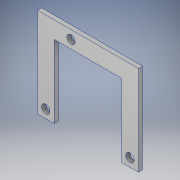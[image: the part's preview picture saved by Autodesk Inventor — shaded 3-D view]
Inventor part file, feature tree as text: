
AUTODESK INVENTOR PART (.ipt)
format: ipt  version: 2018.1 (Build 221171000, 171)  size: 120,832 bytes
history: native  units: mm
features: extrude x2, sketch x2, other x1
ambient origin geometry x8: Origin, YZ Plane, XZ Plane, XY Plane, X Axis, Y Axis, Z Axis, Center Point
bodies: Body1 (feature_tree)
feature tree (5):
  other  "ソリッド1"
  extrude  "押し出し1"  Depth=20.0mm
  extrude  "押し出し2"  Depth=20.0mm
  sketch  "スケッチ1"
  sketch  "スケッチ2"
